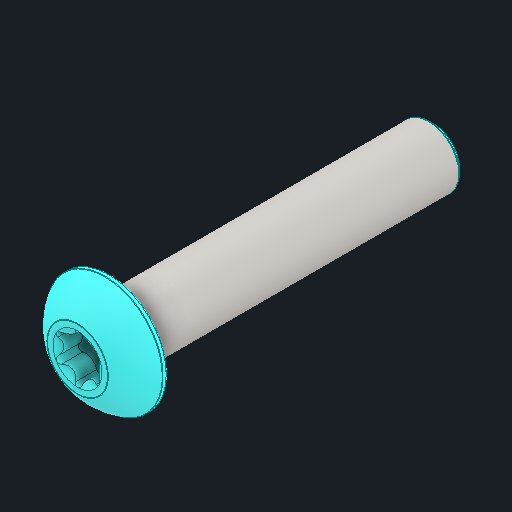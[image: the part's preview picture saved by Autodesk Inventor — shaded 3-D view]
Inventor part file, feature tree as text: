
AUTODESK INVENTOR PART (.ipt)
format: ipt  version: 2025 (Build 290162000, 162)  size: 167,424 bytes
history: native  units: in
note: dims shown in document units (in); Inventor stores cm internally (conversion verified against a paired STEP export)
features: fillet x1
ambient origin geometry x8: Origin, YZ Plane, XZ Plane, XY Plane, X Axis, Y Axis, Z Axis, Center Point
bodies: Solid1 (feature_tree)
feature tree (1):
  fillet  "Fillet1"  [1 undecoded]
note: 1 required parameter value undecoded (feature->parameter linkage not recoverable at this tier; creation-order binding heuristic only, values carry confidence <= 0.55)
